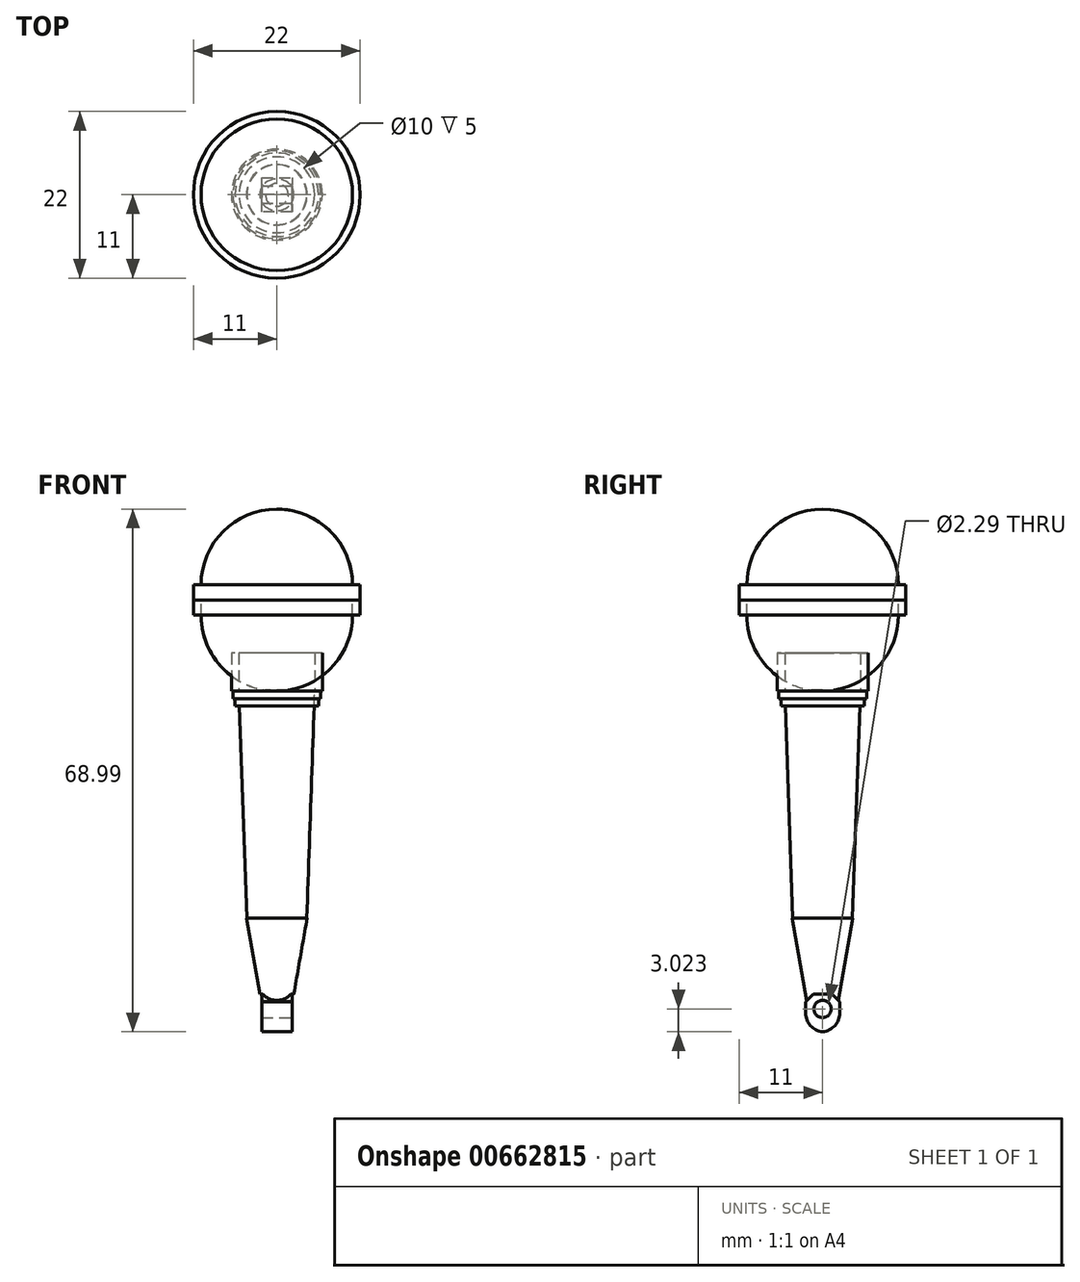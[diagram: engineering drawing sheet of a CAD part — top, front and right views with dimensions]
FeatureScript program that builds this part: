
annotation { "Feature Type Name" : "Feature", "Feature Type Description" : "" }
export const myFeature = defineFeature(function(context is Context, id is Id, definition is map)
    precondition{}
    {
        {
            var Q0;
            Q0=qCreatedBy(makeId("Top.planeOp"),FACE);
            var sketch = newSketch(context, id + "F0", { "sketchPlane" : qUnion([Q0])});
            skCircle(sketch, "E0", {"center": v(0, 0) * mm, "radius": 5 * mm});
            skSolve(sketch);
        }
        {
            var Q0;
            Q0=qSketchRegion(id+"F0",true);
            extrude(context, id + "F1", {"entities" : qUnion([Q0]), "depth" : 30 * mm, "offsetDistance" : 25 * mm});
        }
        {
            var Q0;
            Q0=makeQuery(id+"F1.opExtrude","CAP_FACE",FACE,{"disambiguationData":[OSD([sQuery(id+"F0.wireOp",EDGE,"E0")])],"isStart":false});
            var sketch = newSketch(context, id + "F2", { "sketchPlane" : qUnion([Q0])});
            skCircle(sketch, "E1", {"center": v(0, 0) * mm, "radius": 6 * mm});
            skSolve(sketch);
        }
        {
            var Q0;
            Q0=makeQuery(id+"F2.imprint","IMPRINT",FACE,{"disambiguationData":[TD([[makeQuery(id+"F2.imprint","IMPRINT",EDGE,{"derivedFrom":sQuery(id+"F2.wireOp",EDGE,"E1")}),1.0]])]});
            extrude(context, id + "F3", {"entities" : qUnion([Q0]), "depth" : 5 * mm, "offsetDistance" : 25 * mm});
        }
        {
            var Q0;
            Q0=makeQuery(id+"F1.opExtrude","CAP_FACE",FACE,{"disambiguationData":[OSD([sQuery(id+"F0.wireOp",EDGE,"E0")])],"isStart":false});
            var sketch = newSketch(context, id + "F4", { "sketchPlane" : qUnion([Q0])});
            skCircle(sketch, "E2", {"center": v(0, 0) * mm, "radius": 3.5 * mm});
            skSolve(sketch);
        }
        {
            var Q0;
            Q0=qSketchRegion(id+"F4",true);
            extrude(context, id + "F5", {"entities" : qUnion([Q0]), "operationType" : NewBodyOperationType.ADD, "depth" : -3 * mm, "offsetDistance" : 25 * mm});
        }
        {
            var Q0;
            Q0=makeQuery(id+"F5.boolean.opBoolean","MERGE",FACE,{"derivedFrom":[makeQuery(id+"F1.opExtrude","CAP_FACE",FACE,{"disambiguationData":[OSD([sQuery(id+"F0.wireOp",EDGE,"E0")])],"isStart":false}),makeQuery(id+"F5.opExtrude","CAP_FACE",FACE,{"disambiguationData":[OSD([sQuery(id+"F4.wireOp",EDGE,"E2")])],"isStart":true})]});
            var sketch = newSketch(context, id + "F6", { "sketchPlane" : qUnion([Q0])});
            skCircle(sketch, "E3", {"center": v(0, 0) * mm, "radius": 1.5 * mm});
            skSolve(sketch);
        }
        {
            var Q0;
            Q0=makeQuery(id+"F6.imprint","IMPRINT",FACE,{"disambiguationData":[TD([[makeQuery(id+"F6.imprint","IMPRINT",EDGE,{"derivedFrom":sQuery(id+"F6.wireOp",EDGE,"E3")}),1.0]])]});
            extrude(context, id + "F7", {"entities" : qUnion([Q0]), "operationType" : NewBodyOperationType.ADD, "depth" : 12 * mm, "offsetDistance" : 25 * mm});
        }
        {
            var Q0;
            Q0=makeQuery(id+"F5.boolean.opBoolean","MERGE",FACE,{"derivedFrom":[makeQuery(id+"F1.opExtrude","CAP_FACE",FACE,{"disambiguationData":[OSD([sQuery(id+"F0.wireOp",EDGE,"E0")])],"isStart":false}),makeQuery(id+"F5.opExtrude","CAP_FACE",FACE,{"disambiguationData":[OSD([sQuery(id+"F4.wireOp",EDGE,"E2")])],"isStart":true})]});
            var sketch = newSketch(context, id + "F8", { "sketchPlane" : qUnion([Q0])});
            skLineSegment(sketch, "E4.bottom", {"start": v(-10, 10) * mm, "end": v(10, 10) * mm});
            skLineSegment(sketch, "E4.top", {"start": v(-10, -10) * mm, "end": v(10, -10) * mm});
            skLineSegment(sketch, "E4.left", {"start": v(-10, 10) * mm, "end": v(-10, -10) * mm});
            skLineSegment(sketch, "E4.right", {"start": v(10, 10) * mm, "end": v(10, -10) * mm});
            skPoint(sketch, "E4.middle", {"position": v(0, 0) * mm});
            skSolve(sketch);
        }
        {
            var Q0;
            Q0=qSketchRegion(id+"F8",true);
            extrude(context, id + "F9", {"entities" : qUnion([Q0]), "depth" : 24 * mm, "offsetDistance" : 25 * mm});
        }
        {
            var Q0;
            Q0=makeQuery(id+"F9.opExtrude","CAP_EDGE",EDGE,{"disambiguationData":[OSD([sQuery(id+"F8.wireOp",EDGE,"E4.bottom")])],"isStart":false});
            var Q1;
            Q1=makeQuery(id+"F9.opExtrude","CAP_EDGE",EDGE,{"disambiguationData":[OSD([sQuery(id+"F8.wireOp",EDGE,"E4.right")])],"isStart":false});
            var Q2;
            Q2=makeQuery(id+"F9.opExtrude","CAP_EDGE",EDGE,{"disambiguationData":[OSD([sQuery(id+"F8.wireOp",EDGE,"E4.top")])],"isStart":false});
            var Q3;
            Q3=makeQuery(id+"F9.opExtrude","CAP_EDGE",EDGE,{"disambiguationData":[OSD([sQuery(id+"F8.wireOp",EDGE,"E4.left")])],"isStart":false});
            var Q4;
            Q4=makeQuery(id+"F9.opExtrude","CAP_EDGE",EDGE,{"disambiguationData":[OSD([sQuery(id+"F8.wireOp",EDGE,"E4.top")])],"isStart":true});
            var Q5;
            Q5=makeQuery(id+"F9.opExtrude","CAP_EDGE",EDGE,{"disambiguationData":[OSD([sQuery(id+"F8.wireOp",EDGE,"E4.left")])],"isStart":true});
            var Q6;
            Q6=makeQuery(id+"F9.opExtrude","CAP_EDGE",EDGE,{"disambiguationData":[OSD([sQuery(id+"F8.wireOp",EDGE,"E4.bottom")])],"isStart":true});
            var Q7;
            Q7=makeQuery(id+"F9.opExtrude","CAP_EDGE",EDGE,{"disambiguationData":[OSD([sQuery(id+"F8.wireOp",EDGE,"E4.right")])],"isStart":true});
            var Q8;
            Q8=makeQuery(id+"F9.opExtrude","SWEPT_EDGE",EDGE,{"disambiguationData":[OSD([sQuery(id+"F8.wireOp",EDGE,"E4.bottom"),sQuery(id+"F8.wireOp",EDGE,"E4.right")])]});
            var Q9;
            Q9=makeQuery(id+"F9.opExtrude","SWEPT_EDGE",EDGE,{"disambiguationData":[OSD([sQuery(id+"F8.wireOp",EDGE,"E4.top"),sQuery(id+"F8.wireOp",EDGE,"E4.right")])]});
            var Q10;
            Q10=makeQuery(id+"F9.opExtrude","SWEPT_EDGE",EDGE,{"disambiguationData":[OSD([sQuery(id+"F8.wireOp",EDGE,"E4.top"),sQuery(id+"F8.wireOp",EDGE,"E4.left")])]});
            var Q11;
            Q11=makeQuery(id+"F9.opExtrude","SWEPT_EDGE",EDGE,{"disambiguationData":[OSD([sQuery(id+"F8.wireOp",EDGE,"E4.bottom"),sQuery(id+"F8.wireOp",EDGE,"E4.left")])]});
            fillet(context, id + "F10", {"entities" : qUnion([Q0, Q1, Q2, Q3, Q4, Q5, Q6, Q7, Q8, Q9, Q10, Q11]), "radius" : 10 * mm, "tangentPropagation" : true, "allowEdgeOverflow" : false});
        }
        {
            var Q0;
            Q0=makeQuery(id+"F7.opExtrude","CAP_FACE",FACE,{"disambiguationData":[OSD([sQuery(id+"F6.wireOp",EDGE,"E3")])],"isStart":false});
            var sketch = newSketch(context, id + "F11", { "sketchPlane" : qUnion([Q0])});
            skCircle(sketch, "E5", {"center": v(0, 0) * mm, "radius": 11 * mm});
            skSolve(sketch);
        }
        {
            var Q0;
            Q0=qSketchRegion(id+"F11",true);
            extrude(context, id + "F12", {"entities" : qUnion([Q0]), "operationType" : NewBodyOperationType.ADD, "depth" : 2 * mm, "offsetDistance" : 25 * mm});
        }
        {
            var Q0;
            Q0=qSketchRegion(id+"F11",true);
            extrude(context, id + "F13", {"entities" : qUnion([Q0]), "depth" : -2 * mm, "offsetDistance" : 25 * mm});
        }
        {
            var Q0;
            Q0=makeQuery(id+"F3.opExtrude","CAP_FACE",FACE,{"disambiguationData":[OSD([sQuery(id+"F0.wireOp",EDGE,"E0"),sQuery(id+"F2.wireOp",EDGE,"E1")])],"isStart":true});
            var sketch = newSketch(context, id + "F14", { "sketchPlane" : qUnion([Q0])});
            skCircle(sketch, "E6", {"center": v(0, 0) * mm, "radius": 5.8 * mm});
            skSolve(sketch);
        }
        {
            var Q0;
            Q0=qSketchRegion(id+"F14",true);
            extrude(context, id + "F15", {"entities" : qUnion([Q0]), "depth" : 1 * mm, "offsetDistance" : 25 * mm});
        }
        {
            var Q0;
            Q0=makeQuery(id+"F15.opExtrude","CAP_FACE",FACE,{"disambiguationData":[OSD([sQuery(id+"F14.wireOp",EDGE,"E6")])],"isStart":false});
            var sketch = newSketch(context, id + "F16", { "sketchPlane" : qUnion([Q0])});
            skCircle(sketch, "E7", {"center": v(0, 0) * mm, "radius": 5.5 * mm});
            skSolve(sketch);
        }
        {
            var Q0;
            Q0=qSketchRegion(id+"F16",true);
            extrude(context, id + "F17", {"entities" : qUnion([Q0]), "depth" : 1 * mm, "offsetDistance" : 25 * mm});
        }
        {
            var Q0;
            Q0=qCreatedBy(makeId("Top.planeOp"),FACE);
            var sketch = newSketch(context, id + "F18", { "sketchPlane" : qUnion([Q0])});
            skCircle(sketch, "E8", {"center": v(0, 0) * mm, "radius": 4 * mm});
            skCircle(sketch, "E9", {"center": v(0, 0) * mm, "radius": 3.5 * mm});
            skSolve(sketch);
        }
        {
            var Q0;
            Q0=makeQuery(id+"F1.opExtrude","CAP_EDGE",EDGE,{"disambiguationData":[OSD([sQuery(id+"F0.wireOp",EDGE,"E0")])],"isStart":true});
            chamfer(context, id + "F19", {"entities" : qUnion([Q0]), "chamferType" : ChamferType.OFFSET_ANGLE, "width" : 30 * mm, "oppositeDirection" : false, "angle" : 2 * degree, "tangentPropagation" : true});
        }
        {
            var Q0;
            Q0=makeQuery(id+"F18.imprint","IMPRINT",FACE,{"disambiguationData":[TD([[makeQuery(id+"F18.imprint","IMPRINT",EDGE,{"derivedFrom":sQuery(id+"F18.wireOp",EDGE,"E9")}),1.0]])]});
            var sketch = newSketch(context, id + "F20", { "sketchPlane" : qUnion([Q0])});
            skCircle(sketch, "E10", {"center": v(0, 0) * mm, "radius": 4 * mm});
            skSolve(sketch);
        }
        {
            var Q0;
            Q0=qSketchRegion(id+"F20",true);
            extrude(context, id + "F21", {"entities" : qUnion([Q0]), "operationType" : NewBodyOperationType.ADD, "depth" : -10 * mm, "offsetDistance" : 25 * mm});
        }
        {
            var Q0;
            Q0=makeQuery(id+"F21.opExtrude","CAP_EDGE",EDGE,{"disambiguationData":[OSD([sQuery(id+"F20.wireOp",EDGE,"E10")])],"isStart":false});
            chamfer(context, id + "F22", {"entities" : qUnion([Q0]), "chamferType" : ChamferType.OFFSET_ANGLE, "width" : 10 * mm, "oppositeDirection" : false, "angle" : 10 * degree, "tangentPropagation" : true});
        }
        {
            var Q0;
            Q0=makeQuery(id+"F21.opExtrude","CAP_FACE",FACE,{"disambiguationData":[OSD([sQuery(id+"F20.wireOp",EDGE,"E10")])],"isStart":false});
            var sketch = newSketch(context, id + "F23", { "sketchPlane" : qUnion([Q0])});
            skLineSegment(sketch, "E11", {"start": v(0, -2.24) * mm, "end": v(0, 2.24) * mm});
            skPoint(sketch, "E12.middle", {"position": v(0, 0) * mm});
            skLineSegment(sketch, "E13", {"start": v(0, 2.24) * mm, "end": v(2, 2.24) * mm});
            skLineSegment(sketch, "E14.bottom", {"start": v(2, 2.24) * mm, "end": v(-2, 2.24) * mm});
            skLineSegment(sketch, "E14.top", {"start": v(2, -2.26) * mm, "end": v(-2, -2.26) * mm});
            skLineSegment(sketch, "E14.left", {"start": v(2, 2.24) * mm, "end": v(2, -2.26) * mm});
            skLineSegment(sketch, "E14.right", {"start": v(-2, 2.24) * mm, "end": v(-2, -2.26) * mm});
            skSolve(sketch);
        }
        {
            var Q0;
            Q0=qSketchRegion(id+"F23",true);
            extrude(context, id + "F24", {"entities" : qUnion([Q0]), "operationType" : NewBodyOperationType.ADD, "depth" : 5 * mm, "offsetDistance" : 25 * mm});
        }
        {
            var Q0;
            Q0=makeQuery(id+"F24.opExtrude","CAP_EDGE",EDGE,{"disambiguationData":[OSD([sQuery(id+"F23.wireOp",EDGE,"E14.top")])],"isStart":false});
            var Q1;
            Q1=makeQuery(id+"F24.opExtrude","CAP_EDGE",EDGE,{"disambiguationData":[OSD([sQuery(id+"F23.wireOp",EDGE,"E14.bottom")])],"isStart":false});
            fillet(context, id + "F25", {"entities" : qUnion([Q0, Q1]), "radius" : 2.5 * mm, "tangentPropagation" : true, "allowEdgeOverflow" : false});
        }
        {
            var Q0;
            Q0=makeQuery(id+"F24.opExtrude","CAP_EDGE",EDGE,{"disambiguationData":[OSD([sQuery(id+"F23.wireOp",EDGE,"E14.top")])],"isStart":true});
            var Q1;
            {var subQ0=sQuery(id+"F23.wireOp",EDGE,"E14.bottom");var subQ1=sQuery(id+"F23.wireOp",EDGE,"E14.left");Q1=makeQuery(id+"F24.boolean.opBoolean","SPLIT",EDGE,{"disambiguationData":[TD([makeQuery(id+"F24.opExtrude","SWEPT_FACE",FACE,{"disambiguationData":[OSD([subQ1])]})])],"derivedFrom":makeQuery(id+"F24.opExtrude","CAP_EDGE",EDGE,{"disambiguationData":[OSD([subQ0])],"isStart":true})});}
            chamfer(context, id + "F26", {"entities" : qUnion([Q0, Q1]), "width" : 1 * mm, "tangentPropagation" : true});
        }
        {
            var Q0;
            Q0=makeQuery(id+"F24.opExtrude","SWEPT_FACE",FACE,{"disambiguationData":[OSD([sQuery(id+"F23.wireOp",EDGE,"E14.left")])]});
            var sketch = newSketch(context, id + "F27", { "sketchPlane" : qUnion([Q0])});
            skCircle(sketch, "E15", {"center": v(0, -11.97) * mm, "radius": 1.15 * mm});
            skSolve(sketch);
        }
        {
            var Q0;
            Q0=makeQuery(id+"F27.imprint","IMPRINT",FACE,{"disambiguationData":[TD([[makeQuery(id+"F27.imprint","IMPRINT",EDGE,{"derivedFrom":sQuery(id+"F27.wireOp",EDGE,"E15")}),1.0]])]});
            extrude(context, id + "F28", {"entities" : qUnion([Q0]), "operationType" : NewBodyOperationType.REMOVE, "oppositeDirection" : true, "depth" : 25 * mm, "offsetDistance" : 25 * mm});
        }
    });
